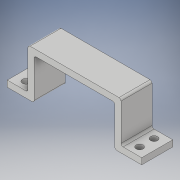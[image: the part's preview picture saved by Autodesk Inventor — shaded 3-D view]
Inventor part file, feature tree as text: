
AUTODESK INVENTOR PART (.ipt)
format: ipt  version: 2017 (Build 210142000, 142)  size: 143,360 bytes
history: native  units: in
note: dims shown in document units (in); Inventor stores cm internally (conversion verified against a paired STEP export)
features: sketch x2, extrude x1, hole x1
ambient origin geometry x8: Origin, YZ Plane, XZ Plane, XY Plane, X Axis, Y Axis, Z Axis, Center Point
bodies: Solid1 (feature_tree)
feature tree (4):
  extrude  "Extrusion1"  Depth=0.1181in
  hole  "Hole1"  [1 undecoded]
  sketch  "Sketch1"  dims[d0=0.1181in d1=0.1181in]
  sketch  "Sketch2"  dims[d2=0.1181in d3=0.1181in d4=0.1181in d5=0.7756in d6=1.5354in d7=0.3937in d8=0.3937in d9=0.0394in d10=0.0394in d11=0.5906in d12=0.0in d13=0.1575in d14=0.1575in d15=0.1575in d16=0.1575in d17=0.1969in d18=0.1969in d19=0.1969in d20=0.1969in d21=0.1339in d22=0.2362in d23=0.1575in d24=0.0787in d25=90.0deg d26=0.315in d27=0.8108in]
note: 1 required parameter value undecoded (feature->parameter linkage not recoverable at this tier; creation-order binding heuristic only, values carry confidence <= 0.55)
